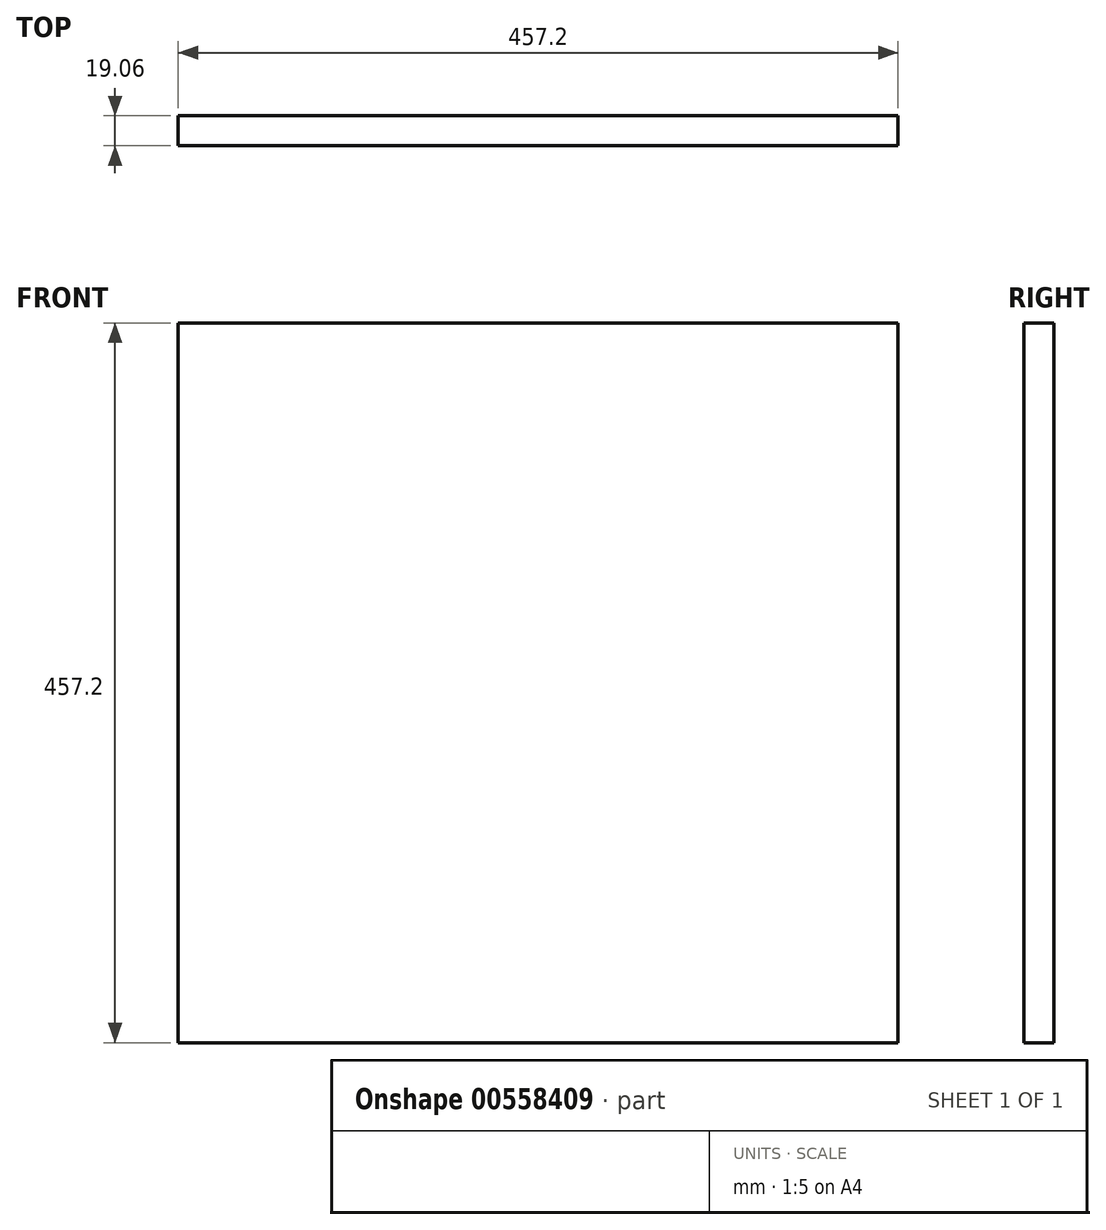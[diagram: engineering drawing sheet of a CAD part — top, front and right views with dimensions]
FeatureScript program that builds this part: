
annotation { "Feature Type Name" : "Feature", "Feature Type Description" : "" }
export const myFeature = defineFeature(function(context is Context, id is Id, definition is map)
    precondition{}
    {
        {
            var Q0;
            Q0=qCreatedBy(makeId("Front.planeOp"),FACE);
            var sketch = newSketch(context, id + "F0", { "sketchPlane" : qUnion([Q0])});
            skLineSegment(sketch, "E0.bottom", {"start": v(228.6, 228.6) * mm, "end": v(-228.6, 228.6) * mm});
            skLineSegment(sketch, "E0.top", {"start": v(228.6, -228.6) * mm, "end": v(-228.6, -228.6) * mm});
            skLineSegment(sketch, "E0.left", {"start": v(228.6, 228.6) * mm, "end": v(228.6, -228.6) * mm});
            skLineSegment(sketch, "E0.right", {"start": v(-228.6, 228.6) * mm, "end": v(-228.6, -228.6) * mm});
            skPoint(sketch, "E0.middle", {"position": v(0, 0) * mm});
            skSolve(sketch);
        }
        {
            var Q0;
            Q0=makeQuery(id+"F0.imprint","IMPRINT",FACE,{"disambiguationData":[TD([[makeQuery(id+"F0.imprint","IMPRINT",EDGE,{"derivedFrom":sQuery(id+"F0.wireOp",EDGE,"E0.bottom")}),1.0]])]});
            extrude(context, id + "F1", {"entities" : qUnion([Q0]), "endBound" : BoundingType.SYMMETRIC, "depth" : 19.05 * mm, "offsetDistance" : 25.4 * mm});
        }
    });
